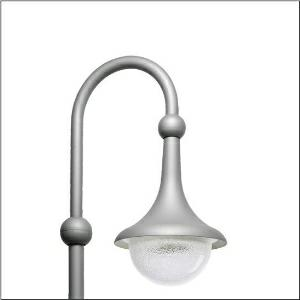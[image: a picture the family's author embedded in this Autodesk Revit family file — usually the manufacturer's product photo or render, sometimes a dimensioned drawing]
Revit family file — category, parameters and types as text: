
# Revit family: kleine_glocke___st1_2a_5xa1573e1b208_4df3
name_source: partatom
category: Lighting Fixtures
units: mm (PartAtom-declared; Revit-internal decimal feet)

## family parameters
Cut with Voids When Loaded = No
Host = Face
Light Source = No
Part Type = Normal
Room Calculation Point = No
Round Connector Dimension = Use Diameter
Shared = No

## types (1)
- --- (1 x LED, 1660 lm, 13.2 W, 3000K)
    Apparent Load = 13 VA
    CIE Flux Codes = 28 64 93 98 100
    Color Rendering = 70
    Color Temperature = 3000K
    Default Elevation = 1800 mm
    Description = Small Bell, mast luminaire, primary light control with 3 zone facetted reflector, of plastic, aluminium vaporised, primary optical cover: enclosure, of PMMA, transparent structured, light distribution: ST1.2a, light emission: direct distribution, primary light characteristic: asymmetric, installation type: suspended mounting, LED, High Power LED, rated luminous flux: 1.660lm, luminous efficacy: 126lm/W, light colour: 730, colour temperature: 3000K, control gear: Plus, control: flexible luminous flux parameterisation, time-dependent luminous flux control, constant luminous flux control, digital communication interface, power reduction, electronic power reduction, mains connection: 230..240V, AC, 50/60Hz, start of lifetime: 13W, end of service life: 14W, reduction: 7W, luminaire housing, bell-shaped, of glass-fibre reinforced polyester, coated, Siteco® metallic grey (DB 702S), please order curved mast extension separately, diameter: 430mm, height: 575mm, mounting height: 2.5..4.0m, protection rating (complete): IP54, insulation class (complete): insulation class II (safety insulation), certification: CE, ENEC, VDE, impact resistance: IK07, standard-compliant lighting for roads and squares, packaging unit: 1 piece

Light Distribution: ST1.2a
    Height = 575 mm
    Lamp = 1 x LED
    Lamp Light Flux = 1660 lm
    Lamp Power = 13.2 W
    Lamp count = 1
    Length = 430 mm
    Luminous efficacy = 126 lm/W
    Manufacturer = Siteco
    ModVariant = No
    Model = 5XA1573E1B208
    Number of Poles = 1
    OnlyDefault = Yes
    Power Factor = 1
    Product Name = Kleine Glocke | ST1.2a
    Product group = mast luminaire | pylon annexe
    ProductGroupID = 6201
    Protection Class = Protection class II
    Protection Degree = IP 54
    RLX_Detail_Level = 1
    RLX_Emergency_Light_Flux = 0 lm
    RLX_Emergency_Type = 0
    RLX_Emergency_Type_DB = No
    RlxData = <blob elided: 52033 chars, md5=53405650>
    Socket = socket
    Standby Power = 0 W
    System Light Flux = 1660 lm
    System Power = 13 W
    Type Comments = factory setting: luminous flux: 100 % | dim-lin: 254 | 249 mA
    Type Image = l_1347695.jpg
    URL = http://relux.com
    VarID = @adj_159026
    Voltage = 0 V
    Weight = 0.00 kg
    Width = 0 mm  [stored 0 ft]

note: [stored X ft] marks values corroborated as IEEE doubles in the binary element streams (Revit-internal decimal feet)

## geometry (parser evidence)
native form markers: Blend x4, Sweep x12
no freeform markers — native parametric forms only
